# Revit family: AL-850
name_source: partatom
category: Plumbing Fixtures
revit_build: Autodesk Revit Architecture 2012 (Build: 20110309_2315(x64)
units: mm (PartAtom-declared; Revit-internal decimal feet)

## types (1)
- AL-850
    Angle regulating valves with sliding wall flanges = 232-10
    Assembly Code = D2010
    CW Connection = Yes
    CWFU = 0
    Cartridge = S-750-1
    Connection tubes = C-M10X1/2
    Cost = 0 $
    Default Elevation = 0' - 0"
    Description = Single lever with pop-up waste + angle valves. 1/2"BSP female inlets
    HW Connection = Yes
    HWFU = 0
    Keynote = Angle regulating valves with sliding wall flanges
    Manufacturer = COBRA
    Material = Chrome - Polished
    Model = AL-850
    Pop up waste = S-380
    Range = Aplos
    Type Comments = SANS 1480
    URL = http://www.cobra.co.za
    Vent Connection = No
    WFU = 0
    Waste Connection = Yes

## geometry (parser evidence)
native form markers: Blend x2
no freeform markers — native parametric forms only
